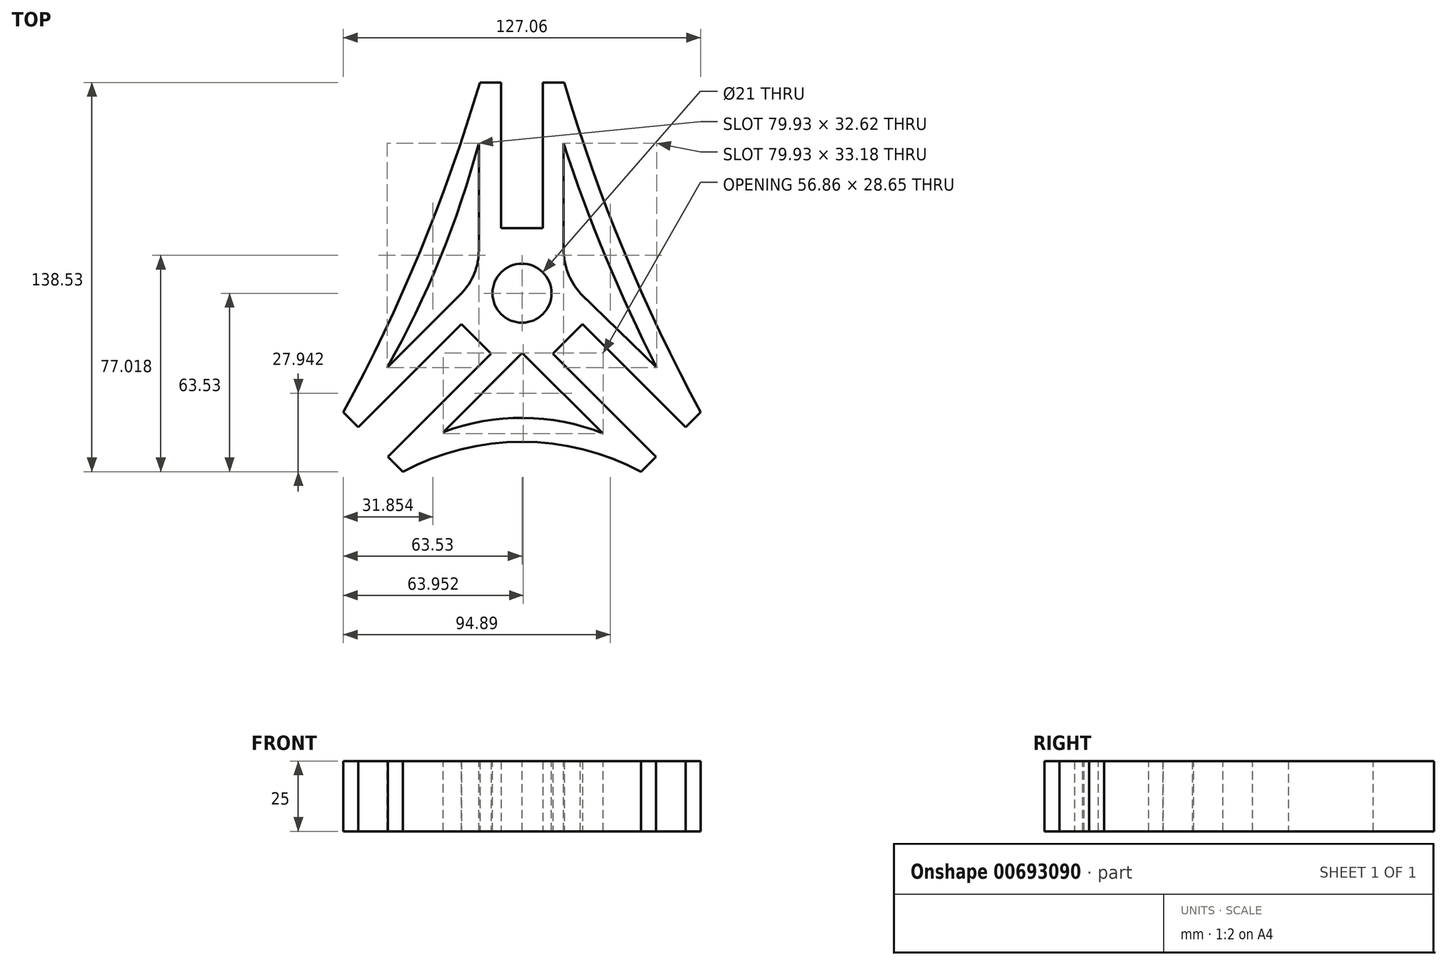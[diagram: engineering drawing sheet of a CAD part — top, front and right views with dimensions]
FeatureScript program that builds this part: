
annotation { "Feature Type Name" : "Feature", "Feature Type Description" : "" }
export const myFeature = defineFeature(function(context is Context, id is Id, definition is map)
    precondition{}
    {
        {
            var Q0;
            Q0=qCreatedBy(makeId("Top.planeOp"),FACE);
            var sketch = newSketch(context, id + "F0", { "sketchPlane" : qUnion([Q0])});
            skLineSegment(sketch, "E0.bottom", {"start": v(75, 75) * mm, "end": v(-75, 75) * mm, "construction": true});
            skLineSegment(sketch, "E0.top", {"start": v(75, -75) * mm, "end": v(-75, -75) * mm, "construction": true});
            skLineSegment(sketch, "E0.left", {"start": v(75, 75) * mm, "end": v(75, -75) * mm, "construction": true});
            skLineSegment(sketch, "E0.right", {"start": v(-75, 75) * mm, "end": v(-75, -75) * mm, "construction": true});
            skLineSegment(sketch, "E1", {"start": v(-15, 75) * mm, "end": v(-7.46, 75) * mm});
            skLineSegment(sketch, "E2", {"start": v(0, 75) * mm, "end": v(0, -75) * mm, "construction": true});
            skLineSegment(sketch, "E3", {"start": v(-75, 0) * mm, "end": v(75, 0) * mm, "construction": true});
            skLineSegment(sketch, "E4.MirrorCS", {"start": v(15, 75) * mm, "end": v(7.46, 75) * mm});
            skLineSegment(sketch, "E5", {"start": v(0, 0) * mm, "end": v(-75, 75) * mm, "construction": true});
            skLineSegment(sketch, "E6", {"start": v(0, 0) * mm, "end": v(75, 75) * mm, "construction": true});
            skLineSegment(sketch, "E7", {"start": v(0, 0) * mm, "end": v(75, -75) * mm, "construction": true});
            skLineSegment(sketch, "E8", {"start": v(0, 0) * mm, "end": v(-75, -75) * mm, "construction": true});
            skLineSegment(sketch, "E9", {"start": v(75, 75) * mm, "end": v(75, 60) * mm});
            skLineSegment(sketch, "E10", {"start": v(75, 75) * mm, "end": v(60, 75) * mm, "construction": true});
            skLineSegment(sketch, "E11", {"start": v(-75, 75) * mm, "end": v(-45, 75) * mm});
            skLineSegment(sketch, "E12", {"start": v(-75, -75) * mm, "end": v(-75, -60) * mm});
            skLineSegment(sketch, "E13", {"start": v(-7.46, 75) * mm, "end": v(-7.46, 23.15) * mm});
            skLineSegment(sketch, "E14", {"start": v(-7.46, 23.15) * mm, "end": v(7.46, 23.15) * mm});
            skLineSegment(sketch, "E15", {"start": v(7.46, 23.15) * mm, "end": v(7.46, 75) * mm});
            skLineSegment(sketch, "E16", {"start": v(-7.46, 23.15) * mm, "end": v(-7.46, 0) * mm, "construction": true});
            skLineSegment(sketch, "E17", {"start": v(-5.27, 5.27) * mm, "end": v(-75, -64.45) * mm, "construction": true});
            skLineSegment(sketch, "E18", {"start": v(-75, -64.45) * mm, "end": v(-64.45, -75) * mm, "construction": true});
            skLineSegment(sketch, "E19", {"start": v(-64.45, -75) * mm, "end": v(5.27, -5.27) * mm, "construction": true});
            skLineSegment(sketch, "E20", {"start": v(5.27, 5.27) * mm, "end": v(75, -64.45) * mm, "construction": true});
            skLineSegment(sketch, "E21", {"start": v(75, -64.45) * mm, "end": v(64.45, -75) * mm, "construction": true});
            skLineSegment(sketch, "E22", {"start": v(64.45, -75) * mm, "end": v(-5.27, -5.27) * mm, "construction": true});
            skLineSegment(sketch, "E23", {"start": v(-21.54, -10.99) * mm, "end": v(-10.99, -21.54) * mm});
            skLineSegment(sketch, "E24", {"start": v(21.54, -10.99) * mm, "end": v(10.99, -21.54) * mm});
            skLineSegment(sketch, "E25", {"start": v(-10.99, -21.54) * mm, "end": v(-47.65, -58.2) * mm});
            skLineSegment(sketch, "E26", {"start": v(-21.54, -10.99) * mm, "end": v(-58.2, -47.65) * mm});
            skLineSegment(sketch, "E27", {"start": v(-47.65, -58.2) * mm, "end": v(-42.32, -63.53) * mm});
            skLineSegment(sketch, "E28", {"start": v(-58.2, -47.65) * mm, "end": v(-63.53, -42.32) * mm});
            skLineSegment(sketch, "E29", {"start": v(10.99, -21.54) * mm, "end": v(47.65, -58.2) * mm});
            skLineSegment(sketch, "E30", {"start": v(21.54, -10.99) * mm, "end": v(58.2, -47.65) * mm});
            skLineSegment(sketch, "E31", {"start": v(47.65, -58.2) * mm, "end": v(42.32, -63.53) * mm});
            skLineSegment(sketch, "E32", {"start": v(58.2, -47.65) * mm, "end": v(63.53, -42.32) * mm});
            skLineSegment(sketch, "E33", {"start": v(-15, 75) * mm, "end": v(-15, 15) * mm});
            skLineSegment(sketch, "E34", {"start": v(15, 75) * mm, "end": v(15, 15) * mm});
            skLineSegment(sketch, "E35", {"start": v(-63.53, -42.32) * mm, "end": v(-21.21, 0) * mm});
            skLineSegment(sketch, "E36", {"start": v(63.53, -42.32) * mm, "end": v(21.21, 0) * mm});
            skLineSegment(sketch, "E37", {"start": v(-42.32, -63.53) * mm, "end": v(0, -21.21) * mm});
            skLineSegment(sketch, "E38", {"start": v(42.32, -63.53) * mm, "end": v(0, -21.21) * mm});
            skArc(sketch, "E39", {"start": v(-21.21, 0) * mm, "mid": v(-16.61, 6.88) * mm, "end": v(-15, 15) * mm});
            skArc(sketch, "E40", {"start": v(15, 15) * mm, "mid": v(16.61, 6.88) * mm, "end": v(21.21, 0) * mm});
            skArc(sketch, "E41", {"start": v(-63.53, -42.32) * mm, "mid": v(-36.19, 15.06) * mm, "end": v(-15, 75) * mm});
            skArc(sketch, "E42", {"start": v(15, 75) * mm, "mid": v(36.2, 15.07) * mm, "end": v(63.53, -42.32) * mm});
            skArc(sketch, "E43", {"start": v(42.32, -63.53) * mm, "mid": v(0, -52.92) * mm, "end": v(-42.32, -63.53) * mm});
            skSolve(sketch);
        }
        {
            var Q0;
            Q0=makeQuery(id+"F0.imprint","IMPRINT",FACE,{"disambiguationData":[TD([[makeQuery(id+"F0.imprint","IMPRINT",EDGE,{"derivedFrom":sQuery(id+"F0.wireOp",EDGE,"E4.MirrorCS")}),1.0]])]});
            extrude(context, id + "F1", {"entities" : qUnion([Q0]), "depth" : 25 * mm, "offsetDistance" : 25 * mm});
        }
        {
            var Q0;
            Q0=makeQuery(id+"F0.imprint","IMPRINT",FACE,{"disambiguationData":[TD([[makeQuery(id+"F0.imprint","IMPRINT",EDGE,{"derivedFrom":sQuery(id+"F0.wireOp",EDGE,"E33")}),-1.0]])]});
            var Q1;
            Q1=makeQuery(id+"F0.imprint","IMPRINT",FACE,{"disambiguationData":[TD([[makeQuery(id+"F0.imprint","IMPRINT",EDGE,{"derivedFrom":sQuery(id+"F0.wireOp",EDGE,"E34")}),1.0]])]});
            var Q2;
            Q2=makeQuery(id+"F0.imprint","IMPRINT",FACE,{"disambiguationData":[TD([[makeQuery(id+"F0.imprint","IMPRINT",EDGE,{"derivedFrom":sQuery(id+"F0.wireOp",EDGE,"E37")}),-1.0]])]});
            extrude(context, id + "F2", {"entities" : qUnion([Q0, Q1, Q2]), "operationType" : NewBodyOperationType.ADD, "depth" : 25 * mm, "offsetDistance" : 25 * mm});
        }
        {
            var Q0;
            {var subQ0=sQuery(id+"F0.wireOp",EDGE,"E38");var subQ1=sQuery(id+"F0.wireOp",EDGE,"E37");var subQ2=sQuery(id+"F0.wireOp",EDGE,"E40");var subQ3=sQuery(id+"F0.wireOp",EDGE,"E36");var subQ4=sQuery(id+"F0.wireOp",EDGE,"E34");var subQ5=sQuery(id+"F0.wireOp",EDGE,"E39");var subQ6=sQuery(id+"F0.wireOp",EDGE,"E35");var subQ7=sQuery(id+"F0.wireOp",EDGE,"E33");Q0=makeQuery(id+"F2.boolean.opBoolean","MERGE",FACE,{"derivedFrom":[makeQuery(id+"F1.opExtrude","CAP_FACE",FACE,{"disambiguationData":[OSD([sQuery(id+"F0.wireOp",EDGE,"E4.MirrorCS"),sQuery(id+"F0.wireOp",EDGE,"E1"),sQuery(id+"F0.wireOp",EDGE,"E13"),sQuery(id+"F0.wireOp",EDGE,"E14"),sQuery(id+"F0.wireOp",EDGE,"E15"),sQuery(id+"F0.wireOp",EDGE,"E23"),sQuery(id+"F0.wireOp",EDGE,"E24"),sQuery(id+"F0.wireOp",EDGE,"E25"),sQuery(id+"F0.wireOp",EDGE,"E26"),sQuery(id+"F0.wireOp",EDGE,"E27"),sQuery(id+"F0.wireOp",EDGE,"E28"),sQuery(id+"F0.wireOp",EDGE,"E29"),sQuery(id+"F0.wireOp",EDGE,"E30"),sQuery(id+"F0.wireOp",EDGE,"E31"),sQuery(id+"F0.wireOp",EDGE,"E32"),subQ7,subQ4,subQ6,subQ3,subQ1,subQ0,subQ5,subQ2])],"isStart":false}),makeQuery(id+"F2.opExtrude","CAP_FACE",FACE,{"disambiguationData":[OSD([subQ7,subQ6,subQ5,sQuery(id+"F0.wireOp",EDGE,"E41")])],"isStart":false}),makeQuery(id+"F2.opExtrude","CAP_FACE",FACE,{"disambiguationData":[OSD([subQ4,subQ3,subQ2,sQuery(id+"F0.wireOp",EDGE,"E42")])],"isStart":false}),makeQuery(id+"F2.opExtrude","CAP_FACE",FACE,{"disambiguationData":[OSD([subQ1,subQ0,sQuery(id+"F0.wireOp",EDGE,"E43")])],"isStart":false})]});}
            var sketch = newSketch(context, id + "F3", { "sketchPlane" : qUnion([Q0])});
            skCircle(sketch, "E44", {"center": v(0, 0) * mm, "radius": 10.5 * mm});
            skSolve(sketch);
        }
        {
            var Q0;
            Q0 = qSketchRegion(id + "F3", true);
            extrude(context, id + "F4", {"entities" : qUnion([Q0]), "operationType" : NewBodyOperationType.REMOVE, "oppositeDirection" : true, "depth" : 25 * mm, "offsetDistance" : 25 * mm});
        }
        {
            var Q0;
            {var subQ0=sQuery(id+"F0.wireOp",EDGE,"E38");var subQ1=sQuery(id+"F0.wireOp",EDGE,"E37");var subQ2=sQuery(id+"F0.wireOp",EDGE,"E40");var subQ3=sQuery(id+"F0.wireOp",EDGE,"E36");var subQ4=sQuery(id+"F0.wireOp",EDGE,"E34");var subQ5=sQuery(id+"F0.wireOp",EDGE,"E39");var subQ6=sQuery(id+"F0.wireOp",EDGE,"E35");var subQ7=sQuery(id+"F0.wireOp",EDGE,"E33");Q0=makeQuery(id+"F2.boolean.opBoolean","MERGE",FACE,{"derivedFrom":[makeQuery(id+"F1.opExtrude","CAP_FACE",FACE,{"disambiguationData":[OSD([sQuery(id+"F0.wireOp",EDGE,"E4.MirrorCS"),sQuery(id+"F0.wireOp",EDGE,"E1"),sQuery(id+"F0.wireOp",EDGE,"E13"),sQuery(id+"F0.wireOp",EDGE,"E14"),sQuery(id+"F0.wireOp",EDGE,"E15"),sQuery(id+"F0.wireOp",EDGE,"E23"),sQuery(id+"F0.wireOp",EDGE,"E24"),sQuery(id+"F0.wireOp",EDGE,"E25"),sQuery(id+"F0.wireOp",EDGE,"E26"),sQuery(id+"F0.wireOp",EDGE,"E27"),sQuery(id+"F0.wireOp",EDGE,"E28"),sQuery(id+"F0.wireOp",EDGE,"E29"),sQuery(id+"F0.wireOp",EDGE,"E30"),sQuery(id+"F0.wireOp",EDGE,"E31"),sQuery(id+"F0.wireOp",EDGE,"E32"),subQ7,subQ4,subQ6,subQ3,subQ1,subQ0,subQ5,subQ2])],"isStart":false}),makeQuery(id+"F2.opExtrude","CAP_FACE",FACE,{"disambiguationData":[OSD([subQ7,subQ6,subQ5,sQuery(id+"F0.wireOp",EDGE,"E41")])],"isStart":false}),makeQuery(id+"F2.opExtrude","CAP_FACE",FACE,{"disambiguationData":[OSD([subQ4,subQ3,subQ2,sQuery(id+"F0.wireOp",EDGE,"E42")])],"isStart":false}),makeQuery(id+"F2.opExtrude","CAP_FACE",FACE,{"disambiguationData":[OSD([subQ1,subQ0,sQuery(id+"F0.wireOp",EDGE,"E43")])],"isStart":false})]});}
            var sketch = newSketch(context, id + "F5", { "sketchPlane" : qUnion([Q0])});
            skArc(sketch, "E45", {"start": v(-47.98, -26.47) * mm, "mid": v(-29.15, 12.46) * mm, "end": v(-15.37, 53.45) * mm});
            skLineSegment(sketch, "E46", {"start": v(-47.98, -26.47) * mm, "end": v(-21.5, 0) * mm});
            skLineSegment(sketch, "E47", {"start": v(-15.37, 53.45) * mm, "end": v(-15.37, 15.18) * mm});
            skArc(sketch, "E48", {"start": v(-21.5, 0) * mm, "mid": v(-16.96, 7) * mm, "end": v(-15.37, 15.18) * mm});
            skArc(sketch, "E49", {"start": v(14.77, 53.45) * mm, "mid": v(29.79, 12.84) * mm, "end": v(47.95, -26.47) * mm});
            skLineSegment(sketch, "E50", {"start": v(14.77, 53.45) * mm, "end": v(14.77, 15.62) * mm});
            skLineSegment(sketch, "E51", {"start": v(47.95, -26.47) * mm, "end": v(20.77, 0) * mm});
            skArc(sketch, "E52", {"start": v(14.77, 15.62) * mm, "mid": v(16.32, 7.25) * mm, "end": v(20.77, 0) * mm});
            skArc(sketch, "E53", {"start": v(28.85, -49.91) * mm, "mid": v(0.46, -44.36) * mm, "end": v(-28, -49.47) * mm});
            skLineSegment(sketch, "E54", {"start": v(-28, -49.47) * mm, "end": v(0, -21.26) * mm});
            skLineSegment(sketch, "E55", {"start": v(0, -21.26) * mm, "end": v(28.85, -49.91) * mm});
            skSolve(sketch);
        }
        {
            var Q0;
            Q0=makeQuery(id+"F5.imprint","IMPRINT",FACE,{"disambiguationData":[TD([[makeQuery(id+"F5.imprint","IMPRINT",EDGE,{"derivedFrom":sQuery(id+"F5.wireOp",EDGE,"E45")}),-1.0]])]});
            var Q1;
            Q1=makeQuery(id+"F5.imprint","IMPRINT",FACE,{"disambiguationData":[TD([[makeQuery(id+"F5.imprint","IMPRINT",EDGE,{"derivedFrom":sQuery(id+"F5.wireOp",EDGE,"E53")}),-1.0]])]});
            var Q2;
            Q2=makeQuery(id+"F5.imprint","IMPRINT",FACE,{"disambiguationData":[TD([[makeQuery(id+"F5.imprint","IMPRINT",EDGE,{"derivedFrom":sQuery(id+"F5.wireOp",EDGE,"E49")}),-1.0]])]});
            extrude(context, id + "F6", {"entities" : qUnion([Q0, Q1, Q2]), "operationType" : NewBodyOperationType.REMOVE, "oppositeDirection" : true, "depth" : 25 * mm, "offsetDistance" : 25 * mm});
        }
    });
